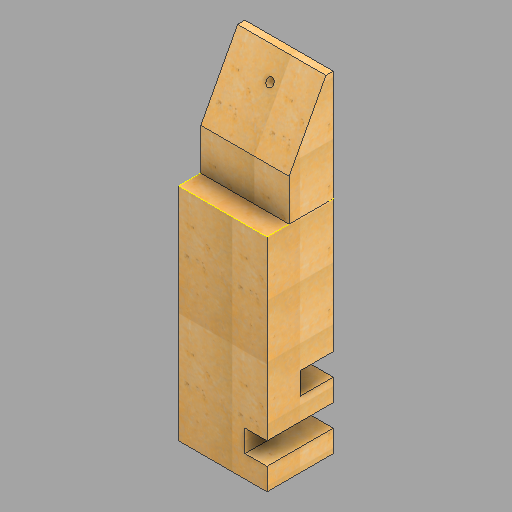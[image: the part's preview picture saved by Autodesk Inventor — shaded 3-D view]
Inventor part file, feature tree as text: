
AUTODESK INVENTOR PART (.ipt)
format: ipt  version: 2023 (Build 270158030, 158C)  size: 312,320 bytes
history: native  units: in
note: dims shown in document units (in); Inventor stores cm internally (conversion verified against a paired STEP export)
features: extrude x4, sketch x4, other x3, split x1, projected_geometry x1
ambient origin geometry x8: Origin, YZ Plane, XZ Plane, XY Plane, X Axis, Y Axis, Z Axis, Center Point
bodies: Solid1 (feature_tree)
feature tree (13):
  extrude  "Extrusion1"  Depth=36.0in
  extrude  "Extrusion2"  Depth=12.0in
  extrude  "Extrusion3"  Depth=22.4972in
  split  "Split1"
  sketch  "Sketch1"  dims[d0=180.0in d1=36.0in]
  sketch  "Sketch2"  dims[d2=120.0in d3=12.0in]
  sketch  "Sketch3"  dims[d4=3.996in d5=22.4972in]
  projected_geometry  "Projected Loop1"
  sketch  "Sketch5"  dims[d6=48.0in d7=0.0in d8=12.0in d9=12.0in d10=12.0in d11=12.0in d12=12.0in d13=12.0in d14=12.0in d15=0.0in d16=12.0in d17=12.0in d18=4.0in d19=0.0in d20=0.0in d21=1.0in d22=0.0in]
  other  "Srf1"
  extrude  "ExtrusionSrf1"  Depth=12.0in
  other  "Bottom"
  other  "Top"
